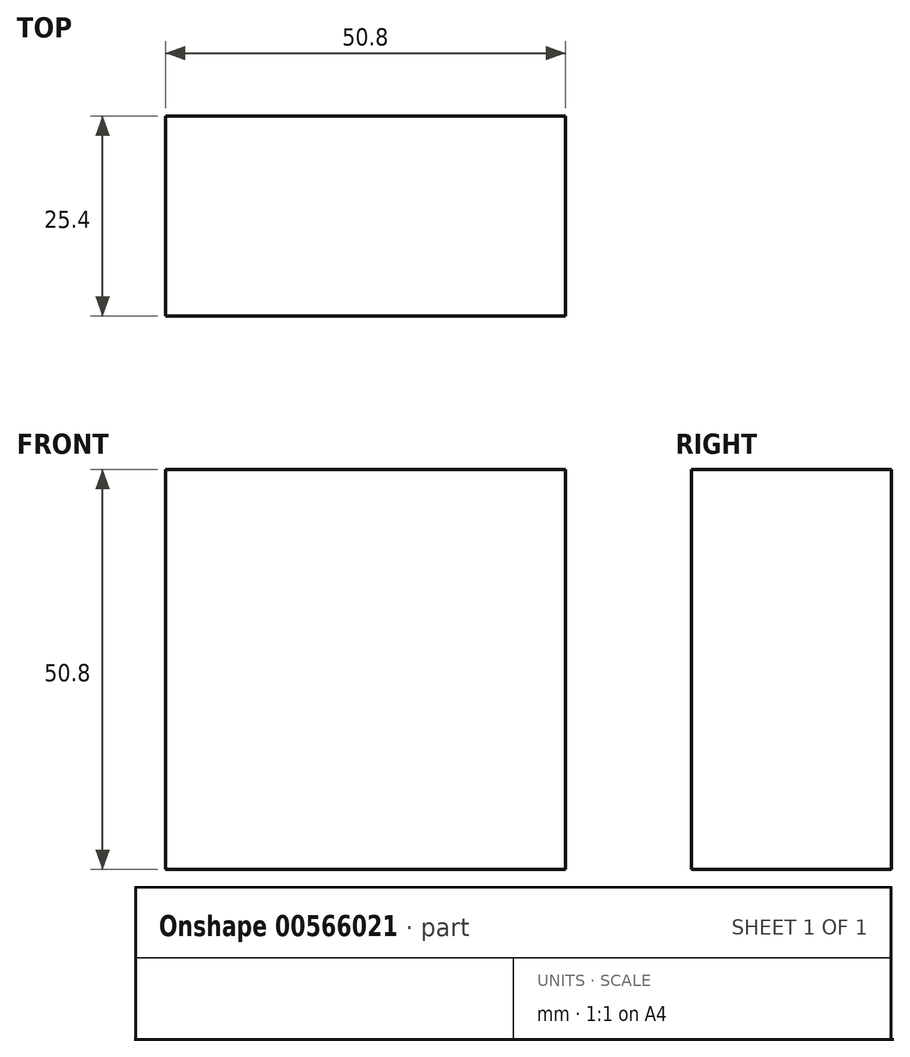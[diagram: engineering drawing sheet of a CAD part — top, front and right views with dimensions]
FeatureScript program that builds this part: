
annotation { "Feature Type Name" : "Feature", "Feature Type Description" : "" }
export const myFeature = defineFeature(function(context is Context, id is Id, definition is map)
    precondition{}
    {
        {
            var Q0;
            Q0=qCreatedBy(makeId("Top.planeOp"),FACE);
            var sketch = newSketch(context, id + "F0", { "sketchPlane" : qUnion([Q0])});
            skLineSegment(sketch, "E0.bottom", {"start": v(-61.73, 41.3) * mm, "end": v(-10.93, 41.3) * mm});
            skLineSegment(sketch, "E0.top", {"start": v(-61.73, 15.9) * mm, "end": v(-10.93, 15.9) * mm});
            skLineSegment(sketch, "E0.left", {"start": v(-61.73, 41.3) * mm, "end": v(-61.73, 15.9) * mm});
            skLineSegment(sketch, "E0.right", {"start": v(-10.93, 41.3) * mm, "end": v(-10.93, 15.9) * mm});
            skSolve(sketch);
        }
        {
            var Q0;
            Q0=makeQuery(id+"F0.imprint","IMPRINT",FACE,{"disambiguationData":[TD([[makeQuery(id+"F0.imprint","IMPRINT",EDGE,{"derivedFrom":sQuery(id+"F0.wireOp",EDGE,"E0.bottom")}),-1.0]])]});
            extrude(context, id + "F1", {"entities" : qUnion([Q0]), "depth" : 50.8 * mm, "offsetDistance" : 25.4 * mm});
        }
    });
